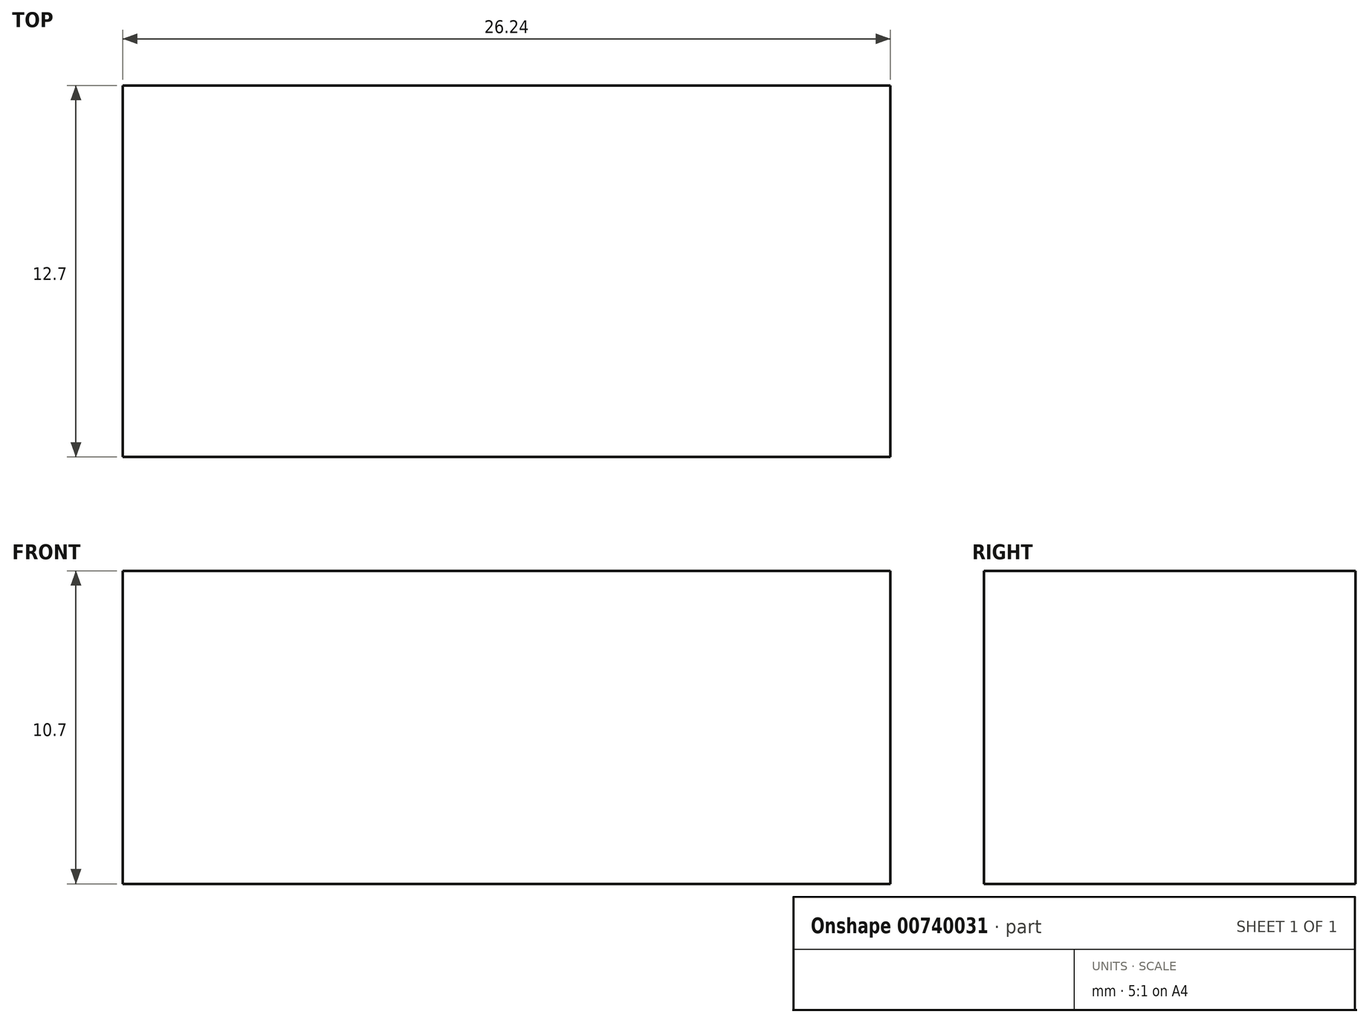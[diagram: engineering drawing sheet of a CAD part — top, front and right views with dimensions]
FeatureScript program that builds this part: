
annotation { "Feature Type Name" : "Feature", "Feature Type Description" : "" }
export const myFeature = defineFeature(function(context is Context, id is Id, definition is map)
    precondition{}
    {
        {
            var Q0;
            Q0=qCreatedBy(makeId("Front.planeOp"),FACE);
            var sketch = newSketch(context, id + "F0", { "sketchPlane" : qUnion([Q0])});
            skLineSegment(sketch, "E0.bottom", {"start": v(-61.8, 45.23) * mm, "end": v(-35.55, 45.23) * mm});
            skLineSegment(sketch, "E0.top", {"start": v(-61.8, 34.53) * mm, "end": v(-35.55, 34.53) * mm});
            skLineSegment(sketch, "E0.left", {"start": v(-61.8, 45.23) * mm, "end": v(-61.8, 34.53) * mm});
            skLineSegment(sketch, "E0.right", {"start": v(-35.55, 45.23) * mm, "end": v(-35.55, 34.53) * mm});
            skSolve(sketch);
        }
        {
            var Q0;
            Q0 = qSketchRegion(id + "F0", true);
            extrude(context, id + "F1", {"entities" : qUnion([Q0]), "depth" : 12.7 * mm, "offsetDistance" : 25.4 * mm});
        }
    });
